# Revit family: xWaste_Receptacle-Bobrick-ClassicSeries-367-60
name_source: partatom
category: Specialty Equipment
revit_build: Autodesk Revit 2014 (Build: 20130308_1515(x64)
units: mm (PartAtom-declared; Revit-internal decimal feet)

## types (1)
- 367-60
    Assembly Code = E20
    Default Elevation = 0"
    Description = ClassicSeries® Interchangeable 12 Gallon Waste Receptacle Module
    Height = 23"
    Installation Type = Secured to cabinet.
    Length = 8"
    Manufacturer = Bobrick Washroom Equipment, Inc.
    Material = Stainless Steel-Bobrick-Type 304-Satin
    Model = 367-60
    Price = Prices may vary. Please consult Manufacturer Representative for most up-to-date price list.
    Product Page URL = http://www.bobrick.com
    Specification = Interchangeable 12 gallon waste receptacle module designed for changing traffic and usage needs. Waste receptacle is type-304 22-gauge stainless steel with satin finish. Front and side edges of bottom and all top edges are hemmed for safe handling. Secured to cabinet with a tumbler lock keyed like other Bobrick washroom accessories. Equipped with interior hooks for optional vinyl liner. Capacity: 12 Gallons. Dimensions: 15 1/8" Wide x 23" High x 8" Deep, Extends 4 1/8" from wall.
    URL = http://www.bobrick.com
    Warranty Information = 1 Year Limited Warranty
    Width = 15 1/8"

## geometry (parser evidence)
native form markers: Sweep x1
no freeform markers — native parametric forms only
